# Revit family: Zumtobel ECOSIGN_PL
name_source: partatom
category: Lighting Fixtures
revit_build: Autodesk Revit 2018 (Build: 20170223_1515(x64)
units: mm (PartAtom-declared; Revit-internal decimal feet)

## family parameters
Cut with Voids When Loaded = No
Host = Face
Light Source = Yes
OmniClass Number = 23.80.70.11
OmniClass Title = Luminaries for Internal Lighting
Part Type = Normal
Room Calculation Point = No
Round Connector Dimension = Use Diameter
Shared = No

## types (8) — shared parameters
Apparent Load = 6 VA
Assembly Code = D5020200
Body = Zumtobel_Metal_White
Color Filter = 16777215
Depth = 54 mm  [stored 0.177165 ft]
Description = Escape sign LED luminaire ceiling surface-mount
Dimming Lamp Color Temperature Shift = <None>
Emit Shape Visible in Rendering = No
Emit from Rectangle Length = 321 mm
Emit from Rectangle Width = 156 mm
Height = 238 mm
Lamp = LED
Manufacturer = Zumtobel Lighting
Tilt Angle = 180.00°
URL = www.zumtobel.de/42180506
Voltage = 230 V
Width = 330 mm
zero-valued in all types: Default Elevation

## per-type parameters (varying)
| type | Escape Sign 1 Back Cover | Escape Sign 1 LR | Escape Sign 1 O | Escape Sign 1 U | Escape Sign 1 UL | Escape Sign 2 LR | Escape Sign 2 O | Escape Sign 2 U | Escape Sign 2 UL | Model | Photometric Web File |
| ECOSIGN AB RZ 2LR | No | No | No | No | No | Yes | No | No | No | 42180506+22166875 | 42180506+22166875_(STD).IES |
| ECOSIGN AB RZ 2U | No | No | No | No | No | No | No | Yes | No | 42180506+22166877 | 42180506+22166875_(STD).IES |
| ECOSIGN AB RZ 2O | No | No | No | No | No | No | Yes | No | No | 42180506+22900372 | 42180506+22166875_(STD).IES |
| ECOSIGN AB RZ 1U | Yes | No | No | Yes | No | No | No | No | No | 42180506+22166876 | 42180506+22166881_(STD).IES |
| ECOSIGN AB RZ 1O | Yes | No | Yes | No | No | No | No | No | No | 42180506+22900372 | 42180506+22166881_(STD).IES |
| ECOSIGN AB RZ 1LR | Yes | Yes | No | No | No | No | No | No | No | 42180506+22166880/22166881 | 42180506+22166881_(STD).IES |
| ECOSIGN aB RZ 2UL | No | No | No | No | No | No | No | No | Yes | 42180506 | 42180506+22166875_(STD).IES |
| ECOSIGN AB RZ 1UL | Yes | No | No | No | Yes | No | No | No | No | 42180506 | 42180506+22166875_(STD).IES |

note: [stored X ft] marks values corroborated as IEEE doubles in the binary element streams (Revit-internal decimal feet)

## geometry (parser evidence)
native form markers: Sweep x2
no freeform markers — native parametric forms only
